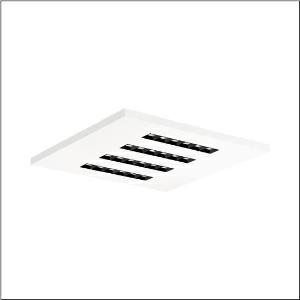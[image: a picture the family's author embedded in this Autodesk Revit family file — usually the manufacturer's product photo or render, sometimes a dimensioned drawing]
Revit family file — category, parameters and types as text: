
# Revit family: silica_21_square_51mx6kdu34w
name_source: partatom
category: Lighting Fixtures
units: mm (PartAtom-declared; Revit-internal decimal feet)

## family parameters
Cut with Voids When Loaded = No
Host = Face
Light Source = No
Part Type = Normal
Room Calculation Point = No
Round Connector Dimension = Use Diameter
Shared = No

## types (1)
- --- (1 x LED, 4600 lm, 31.9 W, 3000K)
    Apparent Load = 32 VA
    CIE Flux Codes = 86 100 100 100 100
    Color Rendering = 80
    Color Temperature = 3000K
    Default Elevation = 1800 mm
    Description = Silica 21 Square, office luminaire, primary light control with lens, of PMMA, primary anti-glare with reflector, of PC, black, CAT 2 (L<= 3000cd/m²), light emission: direct distribution, primary light characteristic: symmetric, installation type: lay-in mounting, LED, rated luminous flux: 4.600lm, luminous efficacy: 144lm/W, light colour: 830, colour temperature: 3000K, control gear: DALI 2, with terminal, 5-pole, mains connection: 220..240V, AC, 50/60Hz, rated input power: 31.9W, luminaire housing, of sheet steel, coated, traffic white (RAL 9016), module: M625, length: 622mm, width: 622mm, height: 33mm, protection rating (complete): IP20, insulation class (complete): insulation class I (protective earthing), certification: CE, ENEC, VDE, permissible operating ambient temperature: -20..+40°C, standard: EN 50419, packaging unit: 1 piece
    Height = 0 mm  [stored 0 ft]
    Lamp = 1 x LED
    Lamp Light Flux = 4600 lm
    Lamp Power = 31.9 W
    Lamp count = 1
    Length = 622 mm
    Luminous efficacy = 144 lm/W
    Manufacturer = Siteco
    ModVariant = No
    Model = 51MX6KDU34W
    Mounting Place = Ceiling
    Mounting Type = Recessed
    Number of Poles = 1
    OnlyDefault = Yes
    Power Factor = 1
    Product Name = Silica 21 Square
    Product group = office luminaire | ceiling recessed
    ProductGroupID = 400
    Protection Class = Protection class I
    Protection Degree = IP 20
    RLX_Detail_Level = 1
    RLX_Emergency_Light_Flux = 0 lm
    RLX_Emergency_Type = 0
    RLX_Emergency_Type_DB = No
    RlxData = <blob elided: 21081 chars, md5=2f46e564>
    Socket = socket
    Standby Power = 0 W
    System Light Flux = 4600 lm
    System Power = 32 W
    Type Comments = factory setting: luminous flux: 100 % | dim-lin: 254 | 430 mA
    Type Image = l_1275207.jpg
    URL = http://relux.com
    VarID = @adj_090593
    Voltage = 0 V
    Weight = 0.00 kg
    Width = 622 mm

note: [stored X ft] marks values corroborated as IEEE doubles in the binary element streams (Revit-internal decimal feet)

## geometry (parser evidence)
native form markers: Blend x4, Sweep x11
no freeform markers — native parametric forms only
